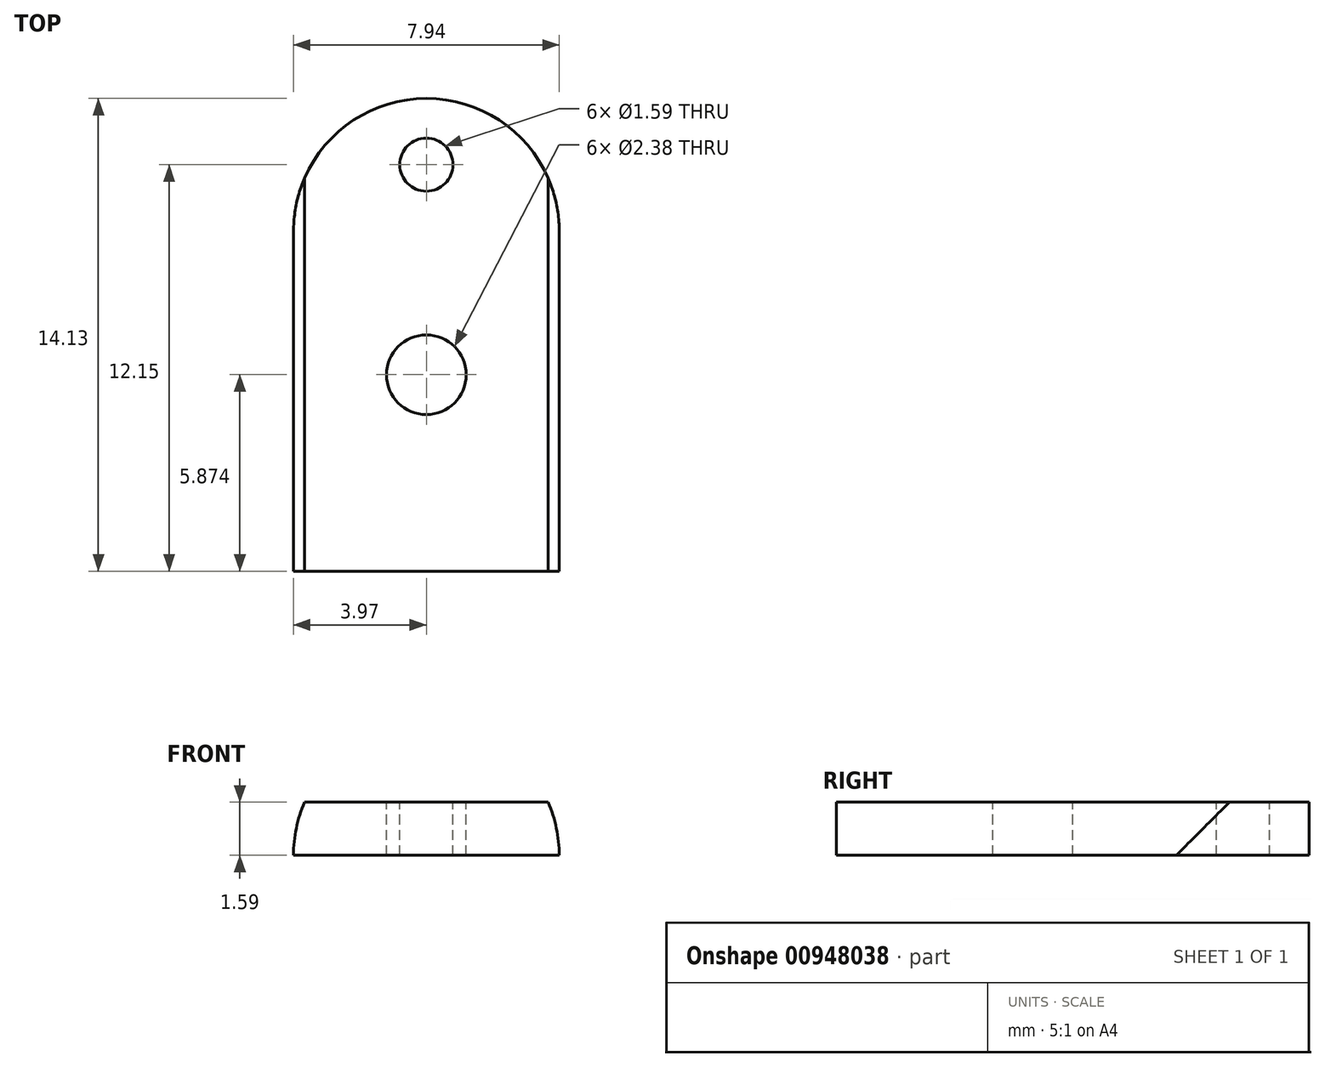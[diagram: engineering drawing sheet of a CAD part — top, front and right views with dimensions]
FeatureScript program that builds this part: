
annotation { "Feature Type Name" : "Feature", "Feature Type Description" : "" }
export const myFeature = defineFeature(function(context is Context, id is Id, definition is map)
    precondition{}
    {
        {
            var Q0;
            Q0=qCreatedBy(makeId("Top.planeOp"),FACE);
            var sketch = newSketch(context, id + "F0", { "sketchPlane" : qUnion([Q0])});
            skLineSegment(sketch, "E0.bottom", {"start": v(-3.97, 5.08) * mm, "end": v(3.97, 5.08) * mm});
            skLineSegment(sketch, "E0.top", {"start": v(-3.97, -5.08) * mm, "end": v(3.97, -5.08) * mm});
            skLineSegment(sketch, "E0.left", {"start": v(-3.97, 5.08) * mm, "end": v(-3.97, -5.08) * mm});
            skLineSegment(sketch, "E0.right", {"start": v(3.97, 5.08) * mm, "end": v(3.97, -5.08) * mm});
            skPoint(sketch, "E0.middle", {"position": v(0, 0) * mm});
            skCircle(sketch, "E1", {"center": v(0, 5.08) * mm, "radius": 3.97 * mm});
            skSolve(sketch);
        }
        {
            var Q0;
            {var subQ0=sQuery(id+"F0.wireOp",EDGE,"E0.bottom");Q0=makeQuery(id+"F0.imprint","IMPRINT",FACE,{"disambiguationData":[TD([[makeQuery(id+"F0.imprint","IMPRINT",EDGE,{"derivedFrom":subQ0}),1.0]])]});}
            var Q1;
            {var subQ0=sQuery(id+"F0.wireOp",EDGE,"E0.bottom");Q1=makeQuery(id+"F0.imprint","IMPRINT",FACE,{"disambiguationData":[TD([[makeQuery(id+"F0.imprint","IMPRINT",EDGE,{"derivedFrom":subQ0}),-1.0]])]});}
            var Q2;
            Q2=makeQuery(id+"F0.imprint","IMPRINT",FACE,{"disambiguationData":[TD([[makeQuery(id+"F0.imprint","IMPRINT",EDGE,{"derivedFrom":sQuery(id+"F0.wireOp",EDGE,"E0.top")}),1.0]])]});
            extrude(context, id + "F1", {"entities" : qUnion([Q0, Q1, Q2]), "depth" : 1.59 * mm, "offsetDistance" : 25.4 * mm});
        }
        {
            var Q0;
            Q0=makeQuery(id+"F1.opExtrude","SWEPT_FACE",FACE,{"disambiguationData":[OSD([sQuery(id+"F0.wireOp",EDGE,"E0.top")])]});
            var sketch = newSketch(context, id + "F2", { "sketchPlane" : qUnion([Q0])});
            skCircle(sketch, "E2", {"center": v(0, 0) * mm, "radius": 3.97 * mm});
            skSolve(sketch);
        }
        {
            var Q0;
            {var subQ1=sQuery(id+"F0.wireOp",EDGE,"E0.top");var subQ2=makeQuery(id+"F1.opExtrude","SWEPT_EDGE",EDGE,{"disambiguationData":[OSD([subQ1,sQuery(id+"F0.wireOp",EDGE,"E0.left")])]});Q0=makeQuery(id+"F2.imprint","IMPRINT",FACE,{"disambiguationData":[TD([[makeQuery(id+"F2.imprint","IMPRINT",EDGE,{"derivedFrom":subQ2}),1.0]])]});}
            var Q1;
            {var subQ1=sQuery(id+"F0.wireOp",EDGE,"E0.top");var subQ2=makeQuery(id+"F1.opExtrude","SWEPT_EDGE",EDGE,{"disambiguationData":[OSD([subQ1,sQuery(id+"F0.wireOp",EDGE,"E0.right")])]});Q1=makeQuery(id+"F2.imprint","IMPRINT",FACE,{"disambiguationData":[TD([[makeQuery(id+"F2.imprint","IMPRINT",EDGE,{"derivedFrom":subQ2}),-1.0]])]});}
            extrude(context, id + "F3", {"entities" : qUnion([Q0, Q1]), "operationType" : NewBodyOperationType.REMOVE, "endBound" : BoundingType.THROUGH_ALL, "oppositeDirection" : true, "depth" : 25.4 * mm, "offsetDistance" : 25.4 * mm});
        }
        {
            var Q0;
            Q0=makeQuery(id+"F1.opExtrude","CAP_FACE",FACE,{"disambiguationData":[OSD([sQuery(id+"F0.wireOp",EDGE,"E0.top"),sQuery(id+"F0.wireOp",EDGE,"E0.left"),sQuery(id+"F0.wireOp",EDGE,"E0.right"),sQuery(id+"F0.wireOp",EDGE,"E1")])],"isStart":false});
            var sketch = newSketch(context, id + "F4", { "sketchPlane" : qUnion([Q0])});
            skCircle(sketch, "E3", {"center": v(0, 0.8) * mm, "radius": 1.2 * mm});
            skPoint(sketch, "E3.centerSnap0", {"position": v(0, 9.05) * mm});
            skPoint(sketch, "E3.centerSnap1", {"position": v(-3.64, 0.8) * mm});
            skCircle(sketch, "E4", {"center": v(0, 7.07) * mm, "radius": 0.8 * mm});
            skSolve(sketch);
        }
        {
            var Q0;
            {var subQ0=sQuery(id+"F4.wireOp",EDGE,"E3");var subQ1=sQuery(id+"F2.wireOp",EDGE,"E2");var subQ2=sQuery(id+"F0.wireOp",EDGE,"E0.top");var subQ3=makeQuery(id+"F1.opExtrude","CAP_EDGE",EDGE,{"disambiguationData":[OSD([subQ2])],"isStart":false});var subQ4=makeQuery(id+"F4.imprint","INTERSECT",VERTEX,{"derivedFrom":[makeQuery(id+"F3.boolean.opBoolean","COPY",EDGE,{"derivedFrom":makeQuery(id+"F3.opExtrude","SWEPT_EDGE",EDGE,{"disambiguationData":[OSD([subQ2,subQ1]),TDD([makeQuery(id+"F2.imprint","INTERSECT",VERTEX,{"disambiguationData":[OD(0.0)],"derivedFrom":[subQ3,subQ1]})])]})}),subQ0]});Q0=makeQuery(id+"F4.imprint","IMPRINT",FACE,{"disambiguationData":[TD([[makeQuery(id+"F4.imprint","IMPRINT",EDGE,{"disambiguationData":[TD([[subQ4,-1.0]])],"derivedFrom":subQ0}),1.0]])]});}
            var Q1;
            Q1=makeQuery(id+"F4.imprint","IMPRINT",FACE,{"disambiguationData":[TD([[makeQuery(id+"F4.imprint","IMPRINT",EDGE,{"derivedFrom":sQuery(id+"F4.wireOp",EDGE,"E4")}),1.0]])]});
            extrude(context, id + "F5", {"entities" : qUnion([Q0, Q1]), "operationType" : NewBodyOperationType.REMOVE, "oppositeDirection" : true, "depth" : 25.4 * mm, "offsetDistance" : 25.4 * mm});
        }
    });
